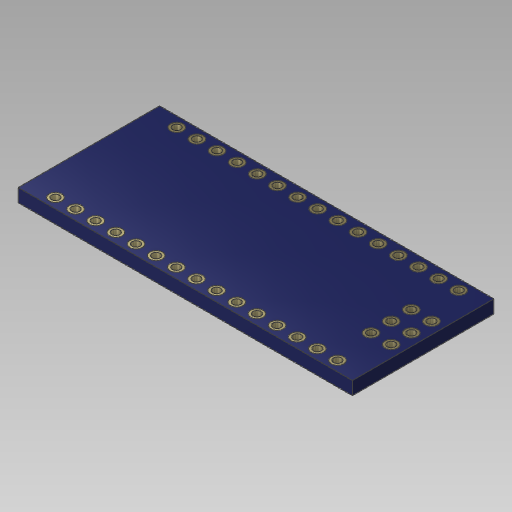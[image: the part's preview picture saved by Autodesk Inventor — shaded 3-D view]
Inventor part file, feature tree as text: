
AUTODESK INVENTOR PART (.ipt)
format: ipt  version: 2020 (Build 240168000, 168)  size: 974,848 bytes
history: native  units: in
note: dims shown in document units (in); Inventor stores cm internally (conversion verified against a paired STEP export)
features: reference x11, sketch x9, other x7, extrude x5, projected_geometry x3, pattern_circular x2, mirror x1, hole x1, sweep x1, pattern_linear x1
ambient origin geometry x8: Origin, YZ Plane, XZ Plane, XY Plane, X Axis, Y Axis, Z Axis, Center Point
bodies: Solid1 (feature_tree)
feature tree (41):
  extrude  "Extrusion1"  Depth=0.702in
  extrude  "Extrusion2"  Depth=0.063in
  mirror  "Mirror1"
  hole  "Hole1"  [1 undecoded]
  extrude  "Extrusion3"  Depth=0.1in
  sweep  "Sweep1"
  sketch  "Sketch8"  dims[d38=0.04in d39=0.75in d40=0.375in d41=0.25in d42=0.5635in d43=1.0in d44=0.8108in d45=0.366in]
  other  "Work Axis1"
  pattern_circular  "Circular Pattern1"  Count=2  [1 undecoded]
  extrude  "Extrusion4"  Depth=0.04in
  pattern_linear  "Rectangular Pattern1"  Spacing1=0.015in  [1 undecoded]
  pattern_circular  "Circular Pattern2"  [2 undecoded]
  extrude  "Extrusion5"  Depth=0.01in
  sketch  "Sketch1"  dims[d0=1.659in d1=0.702in]
  sketch  "Sketch2"  dims[d2=0.065in d3=0.0in d4=0.063in]
  sketch  "Sketch4"  dims[d5=0.135in d6=0.05in]
  projected_geometry  "Projected Loop1"
  sketch  "Sketch5"  dims[d7=0.702in d8=5.9055in d10=0.1in d11=0.3937in d13=1.0in]
  sketch  "Sketch6"  dims[d15=0.0001in d16=0.0in d17=0.0585in d19=0.7874in d21=0.1in d22=0.7874in d24=0.1in]
  sketch  "Sketch7"  dims[d27=0.7874in d29=0.1in d30=0.3937in d32=1.0in]
  projected_geometry  "Projected Loop2"
  sketch  "Sketch9"  dims[d46=0.4in]
  projected_geometry  "Projected Loop3"
  sketch  "Sketch10"  dims[d47=0.045in d48=0.0in d49=0.015in d50=0.005in d51=0.01in d52=0.02in d53=0.2588in d54=3.1496in d56=0.0291in d57=0.3937in d59=1.0in d61=0.015in d62=0.012in d63=0.045in d64=0.0in d65=0.0in d66=1.5748in d67=360.0deg d69=0.005in d70=0.002in d71=0.0001in d72=0.0in d73=0.0141in d74=0.015in d75=3.1496in d77=0.0291in d78=1.5748in d79=360.0deg d81=0.005in d82=0.02in d83=0.008in d84=0.008in d85=0.0984in d86=1.5748in d88=0.0984in d89=0.3937in d91=1.0in d93=0.01in d94=0.01in d95=0.0001in d96=0.0in]
  reference  "Reference1"
  reference  "Reference2"
  reference  "Reference3"
  reference  "Reference4"
  reference  "Reference5"
  reference  "Reference6"
  reference  "Reference7"
  reference  "Reference8"
  reference  "Reference9"
  reference  "Reference10"
  reference  "Reference11"
  other  "Arduino Nano - Soldered.iam"
  other  "Black 0603 - Soldered:1"
  other  "Black 0603 - Soldered:2"
  other  "LED-0603H0.75 - Soldered:1"
  other  "LED-0603H0.75 - Soldered:2"
  other  "Switch:1"
note: 5 required parameter values undecoded (feature->parameter linkage not recoverable at this tier; creation-order binding heuristic only, values carry confidence <= 0.55)
